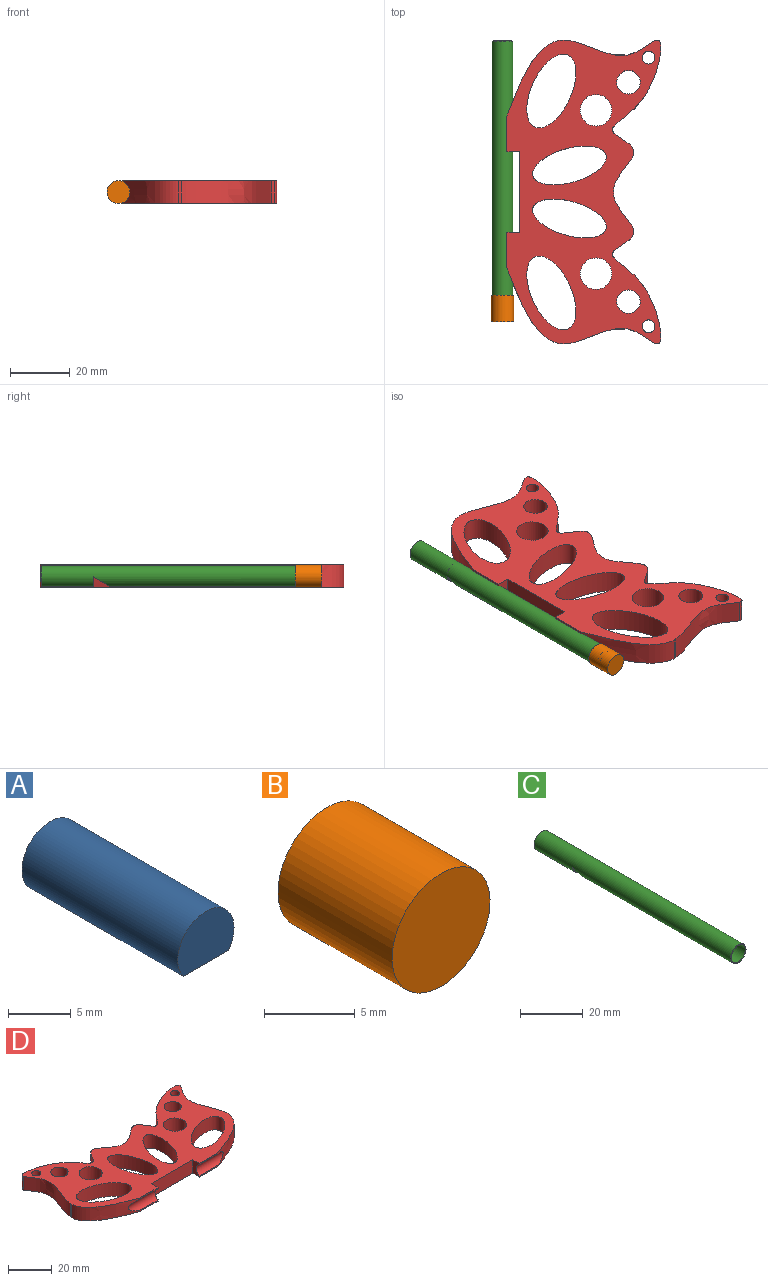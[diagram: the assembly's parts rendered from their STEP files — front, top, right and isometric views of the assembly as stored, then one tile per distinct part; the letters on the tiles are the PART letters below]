
ASSEMBLY  parts=4 mates=3
PART A: 4 faces, bbox 6.3x17.5x5.1 mm
  f0: cylinder r=3.17mm len=17.53mm, axis (0,1,0), area 245.2mm2, adj f1,f2,f3
  f1: plane 6.34x5.08mm, normal (0,-1,0), area 27mm2, adj f0,f3
  f2: plane 6.34x5.06mm, normal (0,1,0), area 27mm2, adj f0,f3
  f3: plane 17.53x5.08mm, normal (0,0,-1), area 89mm2, adj f0,f1,f2
PART B: 5 faces, bbox 7.6x8.9x7.6 mm
  f0: cylinder r=3.81mm len=8.89mm, axis (0,1,0), area 212.8mm2, adj f1,f2
  f1: plane 7.62x7.62mm, normal (0,-1,0), area 45.6mm2, adj f0
  f2: plane 7.62x7.62mm, normal (0,1,0), area 7mm2, adj f0,f3
  f3: cylinder r=3.51mm len=7.01mm, axis (0,-1,0), area 111.9mm2, adj f2,f4
  f4: plane 7.01x7.01mm, normal (0,1,0), area 38.6mm2, adj f3
PART C: 6 faces, bbox 7x88.9x7 mm
  f0: cylinder r=3.17mm len=88.9mm, axis (0,1,0), area 1742.8mm2, adj f2,f3,f4,f5
  f1: cylinder r=3.49mm len=88.9mm, axis (0,1,0), area 1913.3mm2, adj f2,f3,f4,f5
  f2: plane 6.99x6.99mm, normal (0,-1,0), area 6.7mm2, adj f0,f1
  f3: plane 6.99x6.99mm, normal (0,1,0), area 6.7mm2, adj f0,f1
  f4: plane 6.97x3.24mm, normal (0,-1,0), area 3.2mm2, adj f0,f1,f5
  f5: plane 6.97x5.61mm, normal (0,0.5,-0.87), area 6.3mm2, adj f0,f1,f4
PART D: 31 faces, bbox 103.9x52.6x7.6 mm
  f0: plane 11.99x0.65mm, normal (0,-1,0), area 7.8mm2, adj f1,f13,f14,f16
  f1: plane 7.62x4.32mm, normal (1,0,0), area 23.8mm2, adj f0,f2,f3,f14,f15,f16
  f2: plane 11.99x0.64mm, normal (0,-1,0), area 7.7mm2, adj f1,f13,f15,f16
  f3: plane 26.82x7.62mm, normal (0,-1,0), area 204.3mm2, adj f1,f14,f15,f18
  f4: extruded ~50.8x16.22mm, area 470.8mm2, adj f5,f14,f15,f20
  f5: plane 7.62x1.04mm, normal (-1,0,0), area 7.9mm2, adj f4,f6,f14,f15
  f6: extruded ~30.2x7.62mm, area 246.4mm2, adj f5,f7,f14,f15
  f7: plane 7.62x0.83mm, normal (-1,0,0), area 6.3mm2, adj f6,f13,f14,f15
  f8: extruded ~24.67x16.44mm, area 490mm2, adj f14,f15
  f9: extruded ~24.57x13.02mm, area 456.9mm2, adj f14,f15
  f10: cylinder r=2.11mm len=7.62mm, axis (0,0,-1), area 101.2mm2, adj f14,f15
  f11: cylinder r=3.94mm len=7.89mm, axis (0,0,-1), area 188.8mm2, adj f14,f15
  f12: cylinder r=5.28mm len=10.57mm, axis (0,0,-1), area 253mm2, adj f14,f15
  f13: extruded ~25.4x18.73mm, area 226.6mm2, adj f0,f2,f7,f14,f15,f16
  f14: plane 103.89x52.61mm, normal (0,0,1), area 2493.3mm2, adj f0,f1,f3,f4,f5,f6,f7,f8
  f15: plane 103.89x52.61mm, normal (0,0,-1), area 2493.3mm2, adj f1,f2,f3,f4,f5,f6,f7,f8
  f16: cylinder r=3.49mm len=17.31mm, axis (1,0,0), area 122.7mm2, adj f0,f1,f2,f13
  f17: plane 11.99x0.65mm, normal (0,-1,0), area 7.8mm2, adj f14,f18,f29,f30
  f18: plane 7.62x4.32mm, normal (-1,0,0), area 23.8mm2, adj f3,f14,f15,f17,f19,f30
  f19: plane 11.99x0.64mm, normal (0,-1,0), area 7.7mm2, adj f15,f18,f29,f30
  f20: extruded ~50.8x16.22mm, area 470.8mm2, adj f4,f14,f15,f21
  f21: plane 7.62x1.04mm, normal (1,0,0), area 7.9mm2, adj f14,f15,f20,f22
  f22: extruded ~30.2x7.62mm, area 246.4mm2, adj f14,f15,f21,f23
  f23: plane 7.62x0.83mm, normal (1,0,0), area 6.3mm2, adj f14,f15,f22,f29
  f24: extruded ~24.67x16.44mm, area 490mm2, adj f14,f15
  f25: extruded ~24.57x13.02mm, area 456.9mm2, adj f14,f15
  f26: cylinder r=2.11mm len=7.62mm, axis (0,0,-1), area 101.2mm2, adj f14,f15
  f27: cylinder r=3.94mm len=7.89mm, axis (0,0,-1), area 188.8mm2, adj f14,f15
  f28: cylinder r=5.28mm len=10.57mm, axis (0,0,-1), area 253mm2, adj f14,f15
  f29: extruded ~25.4x18.73mm, area 226.6mm2, adj f14,f15,f17,f19,f23,f30
  f30: cylinder r=3.49mm len=17.31mm, axis (-1,0,0), area 122.7mm2, adj f17,f18,f19,f29
PLACE A t=(-25.11,34.01,-23.39)mm
PLACE B rot(axis=(0.57,0.81,0.11),0deg) t=(-25.11,31.56,-23.4)mm
PLACE C rot(axis=(0.57,0.81,0.11),0deg) t=(-25.11,33.94,-23.37)mm
PLACE D rot(axis=(0,0,-1),90deg) t=(-23.64,-16.5,-23.69)mm
MATE cylindrical D.f16 <-> C.f0  axis (0,1,0) through (-25.11,-38.62,-19.88)mm
MATE slider B.f0 <-> C.f0  axis (0,1,0) through (-25.11,-50.99,-19.88)mm
MATE slider A.f0 <-> C.f0  axis (0,1,0) through (-25.11,25.25,-19.88)mm
